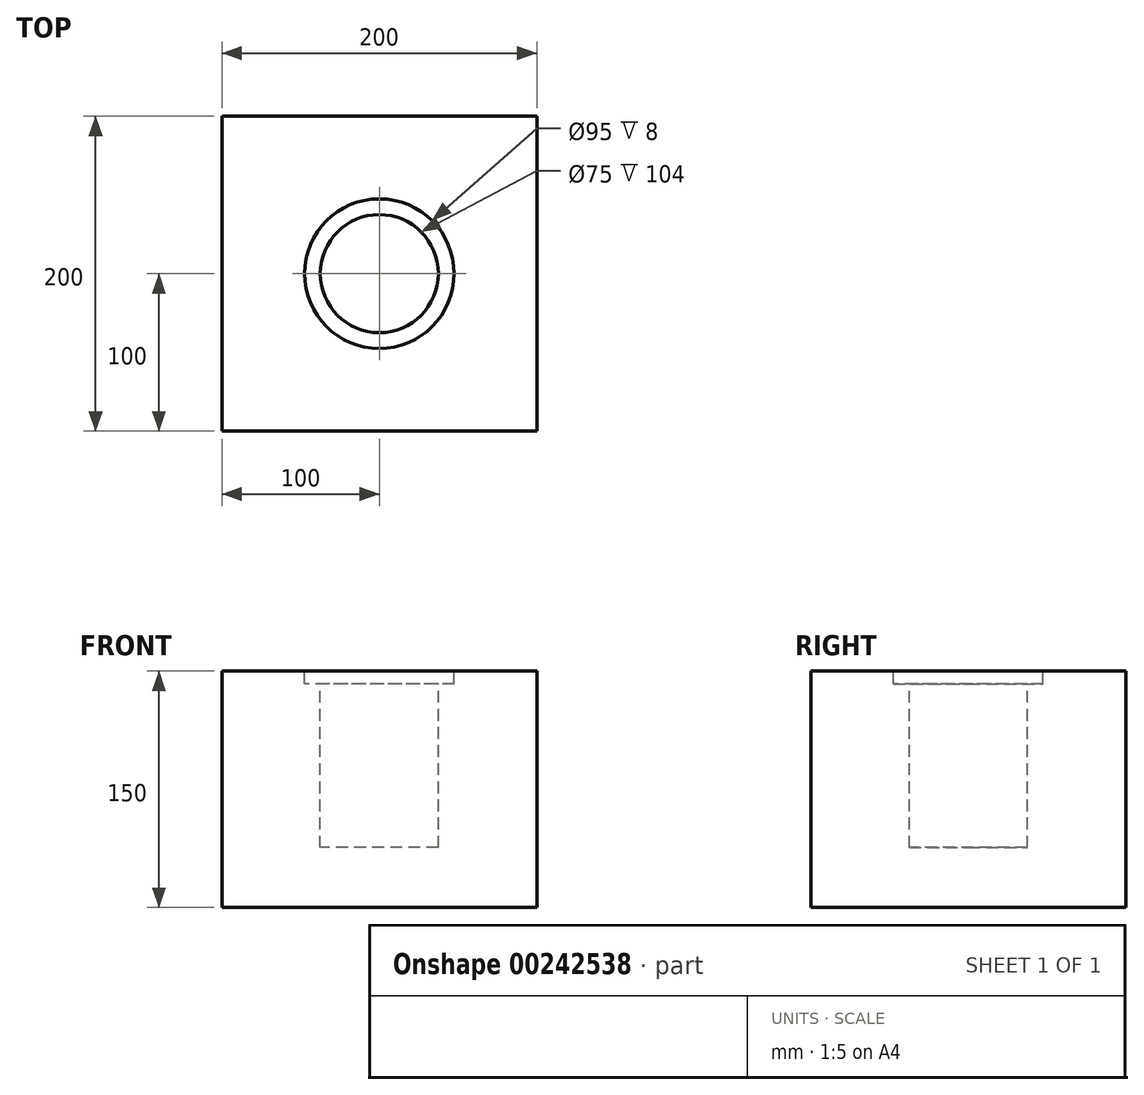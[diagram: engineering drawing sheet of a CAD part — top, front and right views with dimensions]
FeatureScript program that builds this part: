
annotation { "Feature Type Name" : "Feature", "Feature Type Description" : "" }
export const myFeature = defineFeature(function(context is Context, id is Id, definition is map)
    precondition{}
    {
        {
            var Q0;
            Q0=qCreatedBy(makeId("Top.planeOp"),FACE);
            var sketch = newSketch(context, id + "F0", { "sketchPlane" : qUnion([Q0])});
            skLineSegment(sketch, "E0.bottom", {"start": v(-100, 100) * mm, "end": v(100, 100) * mm});
            skLineSegment(sketch, "E0.top", {"start": v(-100, -100) * mm, "end": v(100, -100) * mm});
            skLineSegment(sketch, "E0.left", {"start": v(-100, 100) * mm, "end": v(-100, -100) * mm});
            skLineSegment(sketch, "E0.right", {"start": v(100, 100) * mm, "end": v(100, -100) * mm});
            skPoint(sketch, "E1", {"position": v(0, 100) * mm});
            skPoint(sketch, "E2", {"position": v(-100, 0) * mm});
            skSolve(sketch);
        }
        {
            var Q0;
            Q0=qSketchRegion(id+"F0",true);
            extrude(context, id + "F1", {"entities" : qUnion([Q0]), "depth" : 150 * mm});
        }
        {
            var Q0;
            Q0=makeQuery(id+"F1.opExtrude","CAP_FACE",FACE,{"disambiguationData":[OSD([sQuery(id+"F0.wireOp",EDGE,"E0.bottom"),sQuery(id+"F0.wireOp",EDGE,"E0.top"),sQuery(id+"F0.wireOp",EDGE,"E0.left"),sQuery(id+"F0.wireOp",EDGE,"E0.right")])],"isStart":false});
            var sketch = newSketch(context, id + "F2", { "sketchPlane" : qUnion([Q0])});
            skCircle(sketch, "E3", {"center": v(0, 0) * mm, "radius": 37.5 * mm});
            skSolve(sketch);
        }
        {
            var Q0;
            Q0=qSketchRegion(id+"F2",true);
            extrude(context, id + "F3", {"entities" : qUnion([Q0]), "operationType" : NewBodyOperationType.REMOVE, "oppositeDirection" : true, "depth" : 112 * mm});
        }
        {
            var Q0;
            Q0=makeQuery(id+"F1.opExtrude","CAP_FACE",FACE,{"disambiguationData":[OSD([sQuery(id+"F0.wireOp",EDGE,"E0.bottom"),sQuery(id+"F0.wireOp",EDGE,"E0.top"),sQuery(id+"F0.wireOp",EDGE,"E0.left"),sQuery(id+"F0.wireOp",EDGE,"E0.right")])],"isStart":false});
            var sketch = newSketch(context, id + "F4", { "sketchPlane" : qUnion([Q0])});
            skCircle(sketch, "E4", {"center": v(0, 0) * mm, "radius": 47.5 * mm});
            skSolve(sketch);
        }
        {
            var Q0;
            Q0=qSketchRegion(id+"F4",true);
            extrude(context, id + "F5", {"entities" : qUnion([Q0]), "operationType" : NewBodyOperationType.REMOVE, "oppositeDirection" : true, "depth" : 8 * mm});
        }
    });
